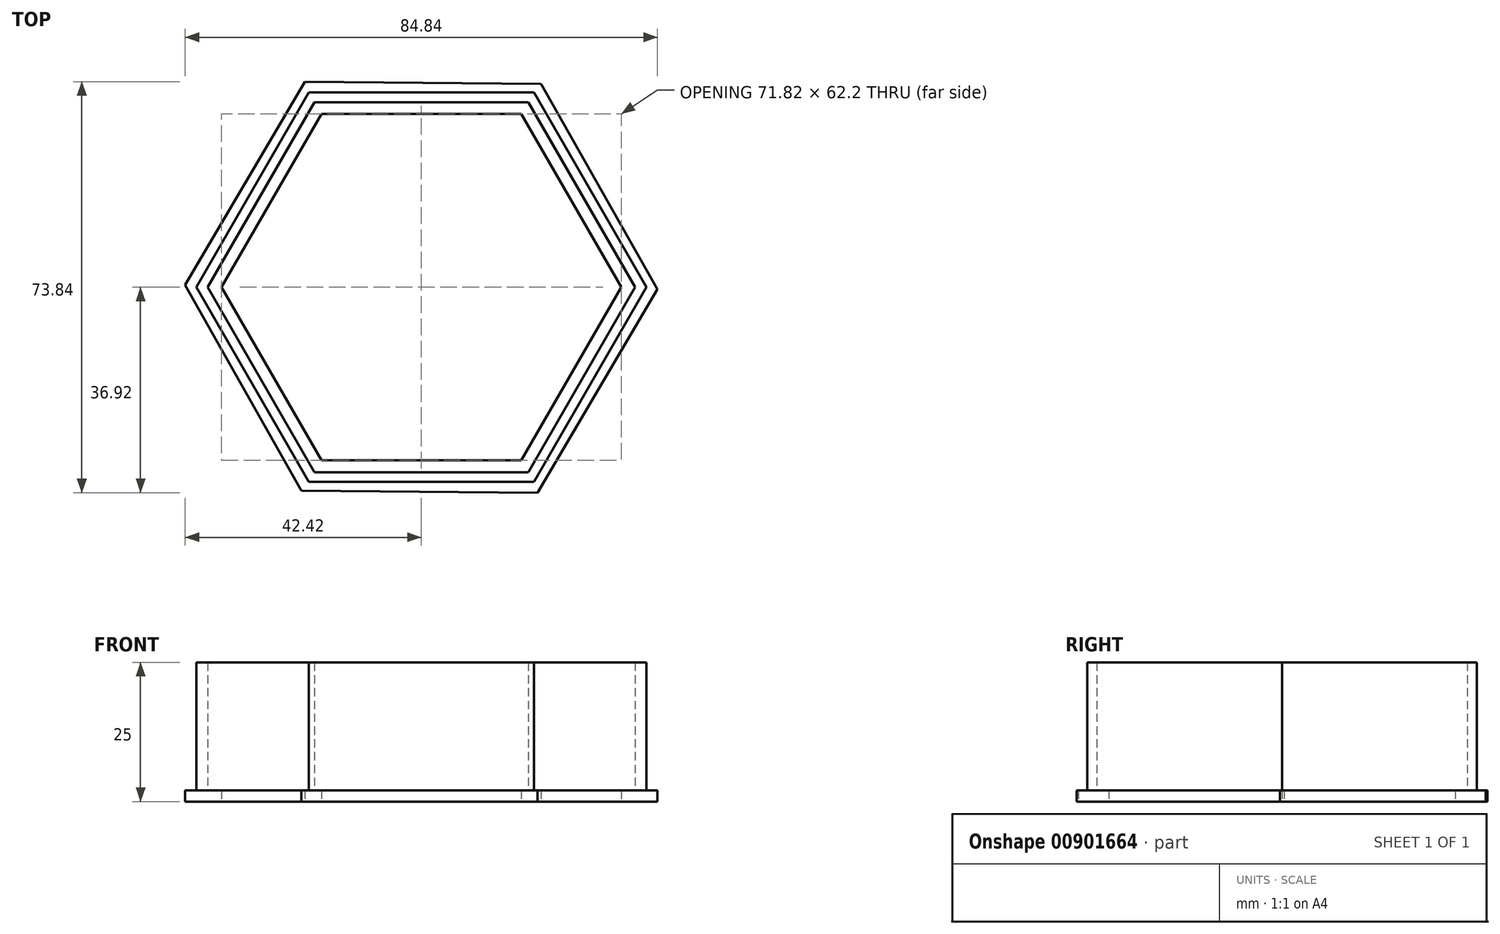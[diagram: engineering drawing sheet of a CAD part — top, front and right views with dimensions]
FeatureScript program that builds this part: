
annotation { "Feature Type Name" : "Feature", "Feature Type Description" : "" }
export const myFeature = defineFeature(function(context is Context, id is Id, definition is map)
    precondition{}
    {
        {
            var Q0;
            Q0=qCreatedBy(makeId("Top.planeOp"),FACE);
            var sketch = newSketch(context, id + "F0", { "sketchPlane" : qUnion([Q0])});
            skCircle(sketch, "E0.cCircle", {"center": v(0, 0) * mm, "radius": 33.25 * mm, "construction": true});
            skLineSegment(sketch, "E0.0", {"start": v(38.4, 0) * mm, "end": v(19.2, -33.25) * mm});
            skLineSegment(sketch, "E0.1", {"start": v(19.2, -33.25) * mm, "end": v(-19.2, -33.25) * mm});
            skLineSegment(sketch, "E0.2", {"start": v(-19.2, -33.25) * mm, "end": v(-38.4, 0) * mm});
            skLineSegment(sketch, "E0.3", {"start": v(-38.4, 0) * mm, "end": v(-19.2, 33.25) * mm});
            skLineSegment(sketch, "E0.4", {"start": v(-19.2, 33.25) * mm, "end": v(19.2, 33.25) * mm});
            skLineSegment(sketch, "E0.5", {"start": v(19.2, 33.25) * mm, "end": v(38.4, 0) * mm});
            skPoint(sketch, "E0.0.midPoint", {"position": v(28.8, -16.63) * mm});
            skCircle(sketch, "E1.cCircle", {"center": v(0, 0) * mm, "radius": 35 * mm, "construction": true});
            skLineSegment(sketch, "E1.0", {"start": v(40.41, 0) * mm, "end": v(20.2, -35) * mm});
            skLineSegment(sketch, "E1.1", {"start": v(20.2, -35) * mm, "end": v(-20.2, -35) * mm});
            skLineSegment(sketch, "E1.2", {"start": v(-20.2, -35) * mm, "end": v(-40.41, 0) * mm});
            skLineSegment(sketch, "E1.3", {"start": v(-40.41, 0) * mm, "end": v(-20.2, 35) * mm});
            skLineSegment(sketch, "E1.4", {"start": v(-20.2, 35) * mm, "end": v(20.2, 35) * mm});
            skLineSegment(sketch, "E1.5", {"start": v(20.2, 35) * mm, "end": v(40.41, 0) * mm});
            skPoint(sketch, "E1.0.midPoint", {"position": v(30.31, -17.5) * mm});
            skSolve(sketch);
        }
        {
            var Q0;
            Q0=makeQuery(id+"F0.imprint","IMPRINT",FACE,{"disambiguationData":[TD([[makeQuery(id+"F0.imprint","IMPRINT",EDGE,{"derivedFrom":sQuery(id+"F0.wireOp",EDGE,"E0.0")}),1.0]])]});
            extrude(context, id + "F1", {"entities" : qUnion([Q0]), "depth" : 25 * mm, "offsetDistance" : 25 * mm});
        }
        {
            var Q0;
            Q0=qCreatedBy(makeId("Top.planeOp"),FACE);
            var sketch = newSketch(context, id + "F2", { "sketchPlane" : qUnion([Q0])});
            skCircle(sketch, "E2.cCircle", {"center": v(0, 0) * mm, "radius": 36.74 * mm, "construction": true});
            skLineSegment(sketch, "E2.0", {"start": v(42.42, -0.37) * mm, "end": v(20.89, -36.92) * mm});
            skLineSegment(sketch, "E2.1", {"start": v(20.89, -36.92) * mm, "end": v(-21.53, -36.55) * mm});
            skLineSegment(sketch, "E2.2", {"start": v(-21.53, -36.55) * mm, "end": v(-42.42, 0.37) * mm});
            skLineSegment(sketch, "E2.3", {"start": v(-42.42, 0.37) * mm, "end": v(-20.89, 36.92) * mm});
            skLineSegment(sketch, "E2.4", {"start": v(-20.89, 36.92) * mm, "end": v(21.53, 36.55) * mm});
            skLineSegment(sketch, "E2.5", {"start": v(21.53, 36.55) * mm, "end": v(42.42, -0.37) * mm});
            skPoint(sketch, "E2.0.midPoint", {"position": v(31.65, -18.64) * mm});
            skSolve(sketch);
        }
        {
            var Q0;
            Q0=makeQuery(id+"F2.imprint","IMPRINT",FACE,{"disambiguationData":[TD([[makeQuery(id+"F2.imprint","IMPRINT",EDGE,{"derivedFrom":sQuery(id+"F2.wireOp",EDGE,"E2.0")}),-1.0]])]});
            extrude(context, id + "F3", {"entities" : qUnion([Q0]), "operationType" : NewBodyOperationType.ADD, "depth" : 2 * mm, "offsetDistance" : 25 * mm});
        }
        {
            var Q0;
            Q0=qCreatedBy(makeId("Top.planeOp"),FACE);
            var sketch = newSketch(context, id + "F4", { "sketchPlane" : qUnion([Q0])});
            skCircle(sketch, "E3.cCircle", {"center": v(0, 0) * mm, "radius": 31.1 * mm, "construction": true});
            skLineSegment(sketch, "E3.0", {"start": v(35.91, 0) * mm, "end": v(17.96, -31.1) * mm});
            skLineSegment(sketch, "E3.1", {"start": v(17.96, -31.1) * mm, "end": v(-17.96, -31.1) * mm});
            skLineSegment(sketch, "E3.2", {"start": v(-17.96, -31.1) * mm, "end": v(-35.91, 0) * mm});
            skLineSegment(sketch, "E3.3", {"start": v(-35.91, 0) * mm, "end": v(-17.96, 31.1) * mm});
            skLineSegment(sketch, "E3.4", {"start": v(-17.96, 31.1) * mm, "end": v(17.96, 31.1) * mm});
            skLineSegment(sketch, "E3.5", {"start": v(17.96, 31.1) * mm, "end": v(35.91, 0) * mm});
            skPoint(sketch, "E3.0.midPoint", {"position": v(26.93, -15.55) * mm});
            skSolve(sketch);
        }
        {
            var Q0;
            Q0 = qSketchRegion(id + "F4", true);
            extrude(context, id + "F5", {"entities" : qUnion([Q0]), "operationType" : NewBodyOperationType.REMOVE, "depth" : 15.1 * mm, "offsetDistance" : 25 * mm});
        }
    });
